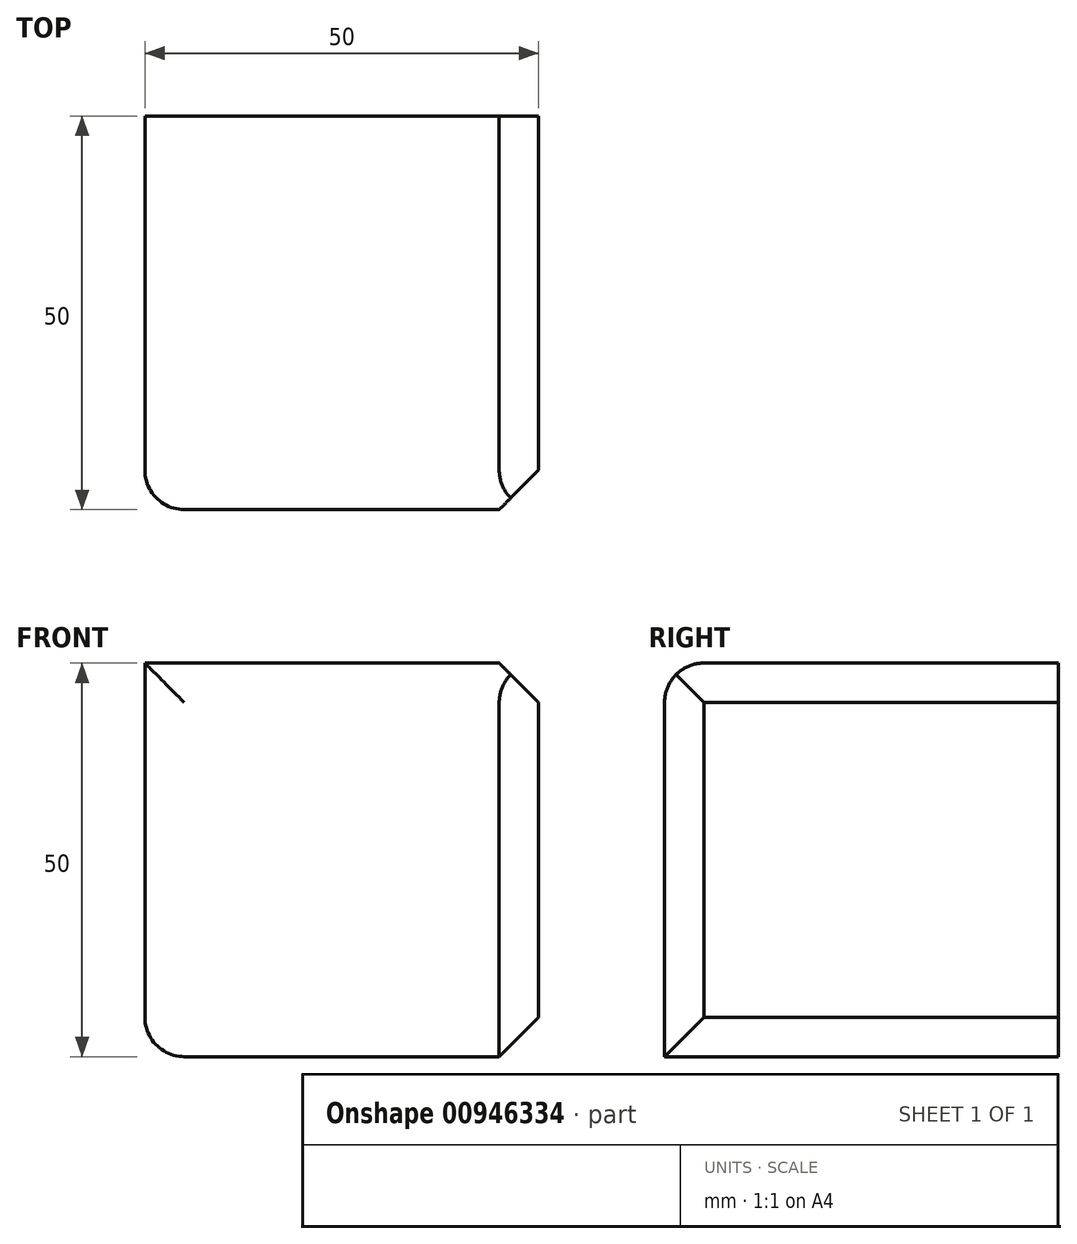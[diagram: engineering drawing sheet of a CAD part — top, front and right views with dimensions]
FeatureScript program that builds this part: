
annotation { "Feature Type Name" : "Feature", "Feature Type Description" : "" }
export const myFeature = defineFeature(function(context is Context, id is Id, definition is map)
    precondition{}
    {
        {
            var Q0;
            Q0=qCreatedBy(makeId("Top.planeOp"),FACE);
            var sketch = newSketch(context, id + "F0", { "sketchPlane" : qUnion([Q0])});
            skLineSegment(sketch, "E0.bottom", {"start": v(-27.78, 30.02) * mm, "end": v(22.22, 30.02) * mm});
            skLineSegment(sketch, "E0.top", {"start": v(-27.78, -19.98) * mm, "end": v(22.22, -19.98) * mm});
            skLineSegment(sketch, "E0.left", {"start": v(-27.78, 30.02) * mm, "end": v(-27.78, -19.98) * mm});
            skLineSegment(sketch, "E0.right", {"start": v(22.22, 30.02) * mm, "end": v(22.22, -19.98) * mm});
            skSolve(sketch);
        }
        {
            var Q0;
            Q0 = qSketchRegion(id + "F0", true);
            extrude(context, id + "F1", {"entities" : qUnion([Q0]), "depth" : 50 * mm, "offsetDistance" : 25 * mm});
        }
        {
            var Q0;
            Q0=makeQuery(id+"F1.opExtrude","CAP_EDGE",EDGE,{"disambiguationData":[OSD([sQuery(id+"F0.wireOp",EDGE,"E0.right")])],"isStart":false});
            var Q1;
            Q1=makeQuery(id+"F1.opExtrude","SWEPT_EDGE",EDGE,{"disambiguationData":[OSD([sQuery(id+"F0.wireOp",EDGE,"E0.top"),sQuery(id+"F0.wireOp",EDGE,"E0.right")])]});
            var Q2;
            Q2=makeQuery(id+"F1.opExtrude","CAP_EDGE",EDGE,{"disambiguationData":[OSD([sQuery(id+"F0.wireOp",EDGE,"E0.right")])],"isStart":true});
            chamfer(context, id + "F2", {"entities" : qUnion([Q0, Q1, Q2]), "width" : 5 * mm, "tangentPropagation" : true});
        }
        {
            var Q0;
            Q0=makeQuery(id+"F1.opExtrude","CAP_EDGE",EDGE,{"disambiguationData":[OSD([sQuery(id+"F0.wireOp",EDGE,"E0.top")])],"isStart":false});
            var Q1;
            Q1=makeQuery(id+"F1.opExtrude","SWEPT_EDGE",EDGE,{"disambiguationData":[OSD([sQuery(id+"F0.wireOp",EDGE,"E0.top"),sQuery(id+"F0.wireOp",EDGE,"E0.left")])]});
            var Q2;
            Q2=makeQuery(id+"F1.opExtrude","CAP_EDGE",EDGE,{"disambiguationData":[OSD([sQuery(id+"F0.wireOp",EDGE,"E0.left")])],"isStart":true});
            fillet(context, id + "F3", {"entities" : qUnion([Q0, Q1, Q2]), "radius" : 5 * mm, "tangentPropagation" : true, "allowEdgeOverflow" : false});
        }
    });
